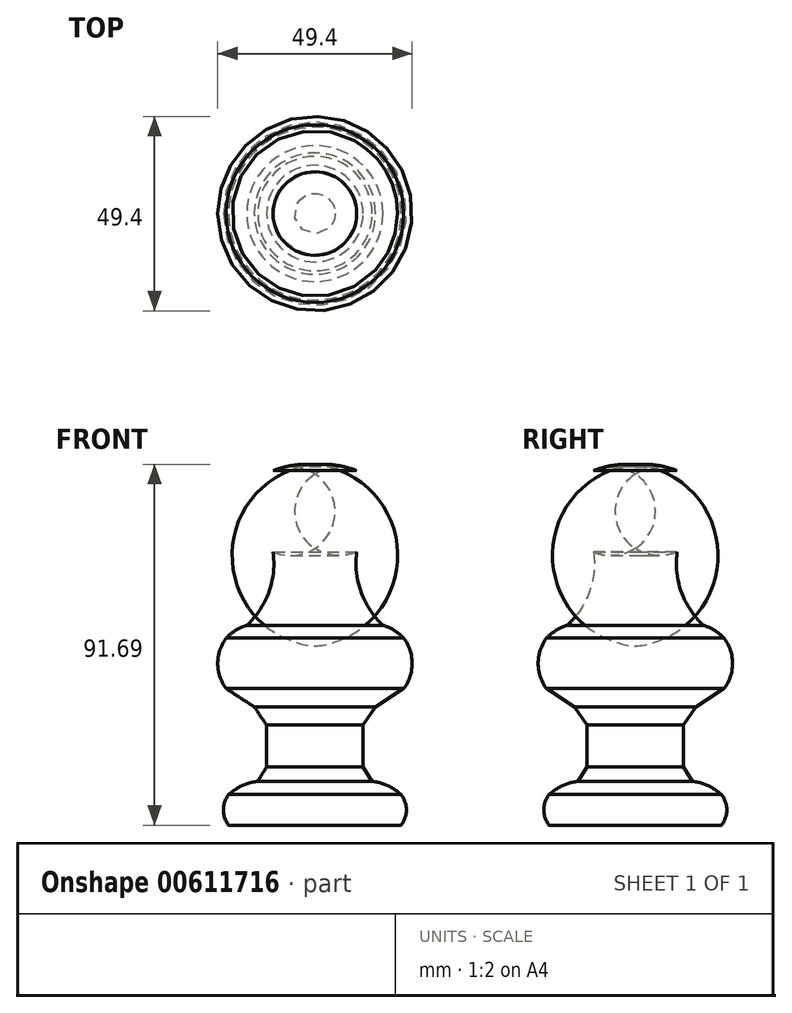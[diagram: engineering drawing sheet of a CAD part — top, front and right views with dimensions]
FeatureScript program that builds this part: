
annotation { "Feature Type Name" : "Feature", "Feature Type Description" : "" }
export const myFeature = defineFeature(function(context is Context, id is Id, definition is map)
    precondition{}
    {
        {
            var Q0;
            Q0=qCreatedBy(makeId("Front.planeOp"),FACE);
            var sketch = newSketch(context, id + "F0", { "sketchPlane" : qUnion([Q0])});
            skLineSegment(sketch, "E0", {"start": v(0, -40.27) * mm, "end": v(-21.91, -40.27) * mm});
            skArc(sketch, "E1", {"start": v(-21.91, -32.5) * mm, "mid": v(-23.25, -36.4) * mm, "end": v(-21.91, -40.27) * mm});
            skArc(sketch, "E2", {"start": v(-14.53, -29.13) * mm, "mid": v(-18.49, -30.23) * mm, "end": v(-21.91, -32.5) * mm});
            skLineSegment(sketch, "E3", {"start": v(-14.53, -29.13) * mm, "end": v(-12.27, -25.5) * mm});
            skLineSegment(sketch, "E4", {"start": v(-12.27, -25.5) * mm, "end": v(-12.27, -14.85) * mm});
            skLineSegment(sketch, "E5", {"start": v(-12.27, -14.85) * mm, "end": v(-15.4, -10.22) * mm});
            skLineSegment(sketch, "E6", {"start": v(-15.4, -10.22) * mm, "end": v(-22.54, -5.59) * mm});
            skArc(sketch, "E7", {"start": v(-22.54, 7.25) * mm, "mid": v(-24.7, 0.83) * mm, "end": v(-22.54, -5.59) * mm});
            skArc(sketch, "E8", {"start": v(-17.3, 10.5) * mm, "mid": v(-20.13, 9.22) * mm, "end": v(-22.54, 7.25) * mm});
            skArc(sketch, "E9", {"start": v(-17.3, 10.5) * mm, "mid": v(-11.68, 19.02) * mm, "end": v(-10.63, 29.16) * mm});
            skArc(sketch, "E10", {"start": v(-10.63, 49.8) * mm, "mid": v(-17.38, 39.48) * mm, "end": v(-10.63, 29.16) * mm});
            skArc(sketch, "E11", {"start": v(0, 51.32) * mm, "mid": v(-5.4, 51.18) * mm, "end": v(-10.63, 49.8) * mm});
            skLineSegment(sketch, "E12", {"start": v(0, 51.32) * mm, "end": v(0, -40.27) * mm});
            skSolve(sketch);
        }
        {
            var Q0;
            Q0 = qSketchRegion(id + "F0", true);
            var Q1;
            Q1=sQuery(id+"F0.wireOp",EDGE,"E9");
            var Q2;
            Q2=sQuery(id+"F0.wireOp",EDGE,"E8");
            var Q3;
            Q3=sQuery(id+"F0.wireOp",EDGE,"E7");
            var Q4;
            Q4=sQuery(id+"F0.wireOp",EDGE,"E6");
            var Q5;
            Q5=sQuery(id+"F0.wireOp",EDGE,"E5");
            var Q6;
            Q6=sQuery(id+"F0.wireOp",EDGE,"E4");
            var Q7;
            Q7=sQuery(id+"F0.wireOp",EDGE,"E3");
            var Q8;
            Q8=sQuery(id+"F0.wireOp",EDGE,"E2");
            var Q9;
            Q9=sQuery(id+"F0.wireOp",EDGE,"E1");
            var Q10;
            Q10=sQuery(id+"F0.wireOp",EDGE,"E0");
            var Q11;
            Q11=sQuery(id+"F0.wireOp",EDGE,"E10");
            var Q12;
            Q12=sQuery(id+"F0.wireOp",EDGE,"E11");
            var Q13;
            Q13=sQuery(id+"F0.wireOp",EDGE,"E12");
            revolve(context, id + "F1", {"bodyType" : ToolBodyType.SURFACE, "entities" : qUnion([Q0]), "surfaceEntities" : qUnion([Q1, Q2, Q3, Q4, Q5, Q6, Q7, Q8, Q9, Q10, Q11, Q12]), "axis" : qUnion([Q13]), "revolveType" : RevolveType.FULL});
        }
    });
